# Revit family: MB-1P
name_source: partatom
category: Furniture
revit_build: Autodesk Revit 2018 (Build: 20170223_1515(x64)
units: mm (PartAtom-declared; Revit-internal decimal feet)

## family parameters
Always vertical = Yes
Cut with Voids When Loaded = No
Host = Wall
Room Calculation Point = No
Shared = No

## types (10) — shared parameters
Hauteur = 872 mm  [stored 2.86089 ft]
Hauteur de plinthe = 100 mm  [stored 0.328084 ft]

## per-type parameters (varying)
| type | Façade | Finition | Largeur | Profondeur |
| 340 x 500 x 872 mm | Bois - Mélaminé jaune/vert | Bois - Mélaminé jaune pastel | 340 mm  [stored 1.11549 ft] | 500 mm  [stored 1.64042 ft] |
| 420 x 500 x 872 mm | Bois - Mélaminé jaune/vert | Bois - Mélaminé jaune pastel | 420 mm  [stored 1.37795 ft] | 500 mm  [stored 1.64042 ft] |
| 520 x 500 x 872 mm | Bois - Mélaminé jaune/vert | Bois - Mélaminé jaune pastel | 520 mm  [stored 1.70604 ft] | 500 mm  [stored 1.64042 ft] |
| 640 x 500 x 872 mm | Bois - Mélaminé jaune/vert | Bois - Mélaminé jaune pastel | 640 mm  [stored 2.09974 ft] | 500 mm  [stored 1.64042 ft] |
| 600 x 200 x 870 mm | Bois - Cerisier | Bois - Cerisier | 200 mm  [stored 0.656168 ft] | 600 mm |
| 600 x 1200  x 870 mm 2 | Bois - Cerisier | Bois - Cerisier | 1200 mm | 600 mm |
| 600 x 300x 870 mm | Bois - Cerisier | Bois - Cerisier | 300 mm | 600 mm |
| 600 x 600 x 870 mm | Bois - Cerisier | Bois - Cerisier | 600 mm | 600 mm |
| 500x 300 x 870  mm | Bois - Cerisier | Bois - Cerisier | 300 mm | 500 mm  [stored 1.64042 ft] |
| 500 x 600 x 870 mm | Bois - Cerisier | Bois - Cerisier | 600 mm | 500 mm  [stored 1.64042 ft] |

note: [stored X ft] marks values corroborated as IEEE doubles in the binary element streams (Revit-internal decimal feet)

## geometry (parser evidence)
native form markers: Blend x2
no freeform markers — native parametric forms only
